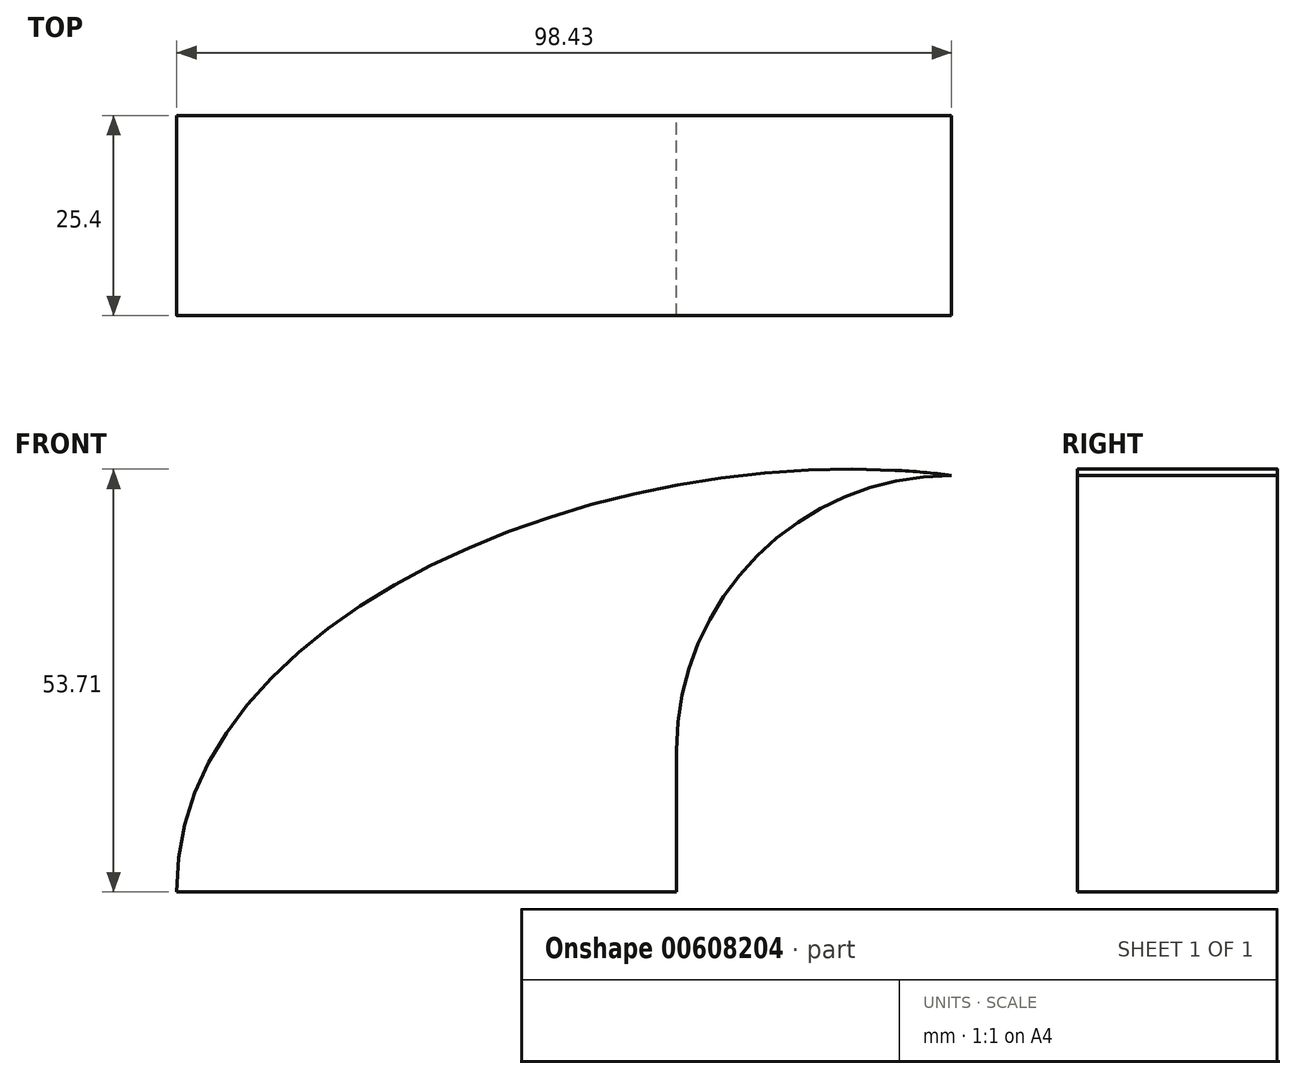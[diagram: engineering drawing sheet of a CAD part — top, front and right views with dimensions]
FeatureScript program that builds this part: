
annotation { "Feature Type Name" : "Feature", "Feature Type Description" : "" }
export const myFeature = defineFeature(function(context is Context, id is Id, definition is map)
    precondition{}
    {
        {
            var Q0;
            Q0=qCreatedBy(makeId("Front.planeOp"),FACE);
            var sketch = newSketch(context, id + "F0", { "sketchPlane" : qUnion([Q0])});
            skLineSegment(sketch, "E0.bottom", {"start": v(41.28, -9.52) * mm, "end": v(-41.28, -9.53) * mm});
            skLineSegment(sketch, "E0.top", {"start": v(41.28, 9.53) * mm, "end": v(-41.28, 9.52) * mm});
            skLineSegment(sketch, "E0.left", {"start": v(41.28, -9.52) * mm, "end": v(41.28, 9.53) * mm});
            skLineSegment(sketch, "E0.right", {"start": v(-41.28, -9.53) * mm, "end": v(-41.28, 9.52) * mm});
            skPoint(sketch, "E0.middle", {"position": v(0, 0) * mm});
            skLineSegment(sketch, "E1.bottom", {"start": v(100.76, 38.1) * mm, "end": v(49.96, 38.1) * mm});
            skLineSegment(sketch, "E1.top", {"start": v(100.76, 66.68) * mm, "end": v(49.96, 66.68) * mm});
            skLineSegment(sketch, "E1.left", {"start": v(100.76, 38.1) * mm, "end": v(100.76, 66.68) * mm});
            skLineSegment(sketch, "E1.right", {"start": v(49.96, 38.1) * mm, "end": v(49.96, 66.68) * mm});
            skPoint(sketch, "E1.middle", {"position": v(75.36, 52.39) * mm});
            skLineSegment(sketch, "E2", {"start": v(41.28, 9.53) * mm, "end": v(41.28, 27.5) * mm});
            skArc(sketch, "E3", {"start": v(41.28, 27.5) * mm, "mid": v(45.92, 38.73) * mm, "end": v(57.15, 43.38) * mm});
            skLineSegment(sketch, "E4", {"start": v(57.15, 43.38) * mm, "end": v(75.33, 43.38) * mm});
            skLineSegment(sketch, "E5.0", {"start": v(57.15, 62.43) * mm, "end": v(75.33, 62.43) * mm});
            skArc(sketch, "E5.1", {"start": v(22.23, 27.5) * mm, "mid": v(32.45, 52.2) * mm, "end": v(57.15, 62.43) * mm});
            skLineSegment(sketch, "E5.2", {"start": v(22.23, 9.53) * mm, "end": v(22.23, 27.5) * mm});
            skFitSpline(sketch, "E6", {"points": [v(-41.28, 9.52) * mm, v(57.15, 62.43) * mm], "startDerivative": vector(-1.27, 106.92) * mm, "endDerivative": vector(127.65, -16.25) * mm});
            skSolve(sketch);
        }
        {
            var Q0;
            {var subQ0=sQuery(id+"F0.wireOp",EDGE,"E6");var subQ1=sQuery(id+"F0.wireOp",EDGE,"E1.right");var subQ2=makeQuery(id+"F0.imprint","INTERSECT",VERTEX,{"derivedFrom":[subQ1,subQ0]});Q0=makeQuery(id+"F0.imprint","IMPRINT",FACE,{"disambiguationData":[TD([[makeQuery(id+"F0.imprint","IMPRINT",EDGE,{"disambiguationData":[TD([[subQ2,1.0]])],"derivedFrom":subQ1}),-1.0]])]});}
            var Q1;
            {var subQ0=sQuery(id+"F0.wireOp",EDGE,"E5.2");Q1=makeQuery(id+"F0.imprint","IMPRINT",FACE,{"disambiguationData":[TD([[makeQuery(id+"F0.imprint","IMPRINT",EDGE,{"derivedFrom":subQ0}),1.0]])]});}
            extrude(context, id + "F1", {"entities" : qUnion([Q0, Q1]), "depth" : 25.4 * mm, "offsetDistance" : 25.4 * mm});
        }
    });
